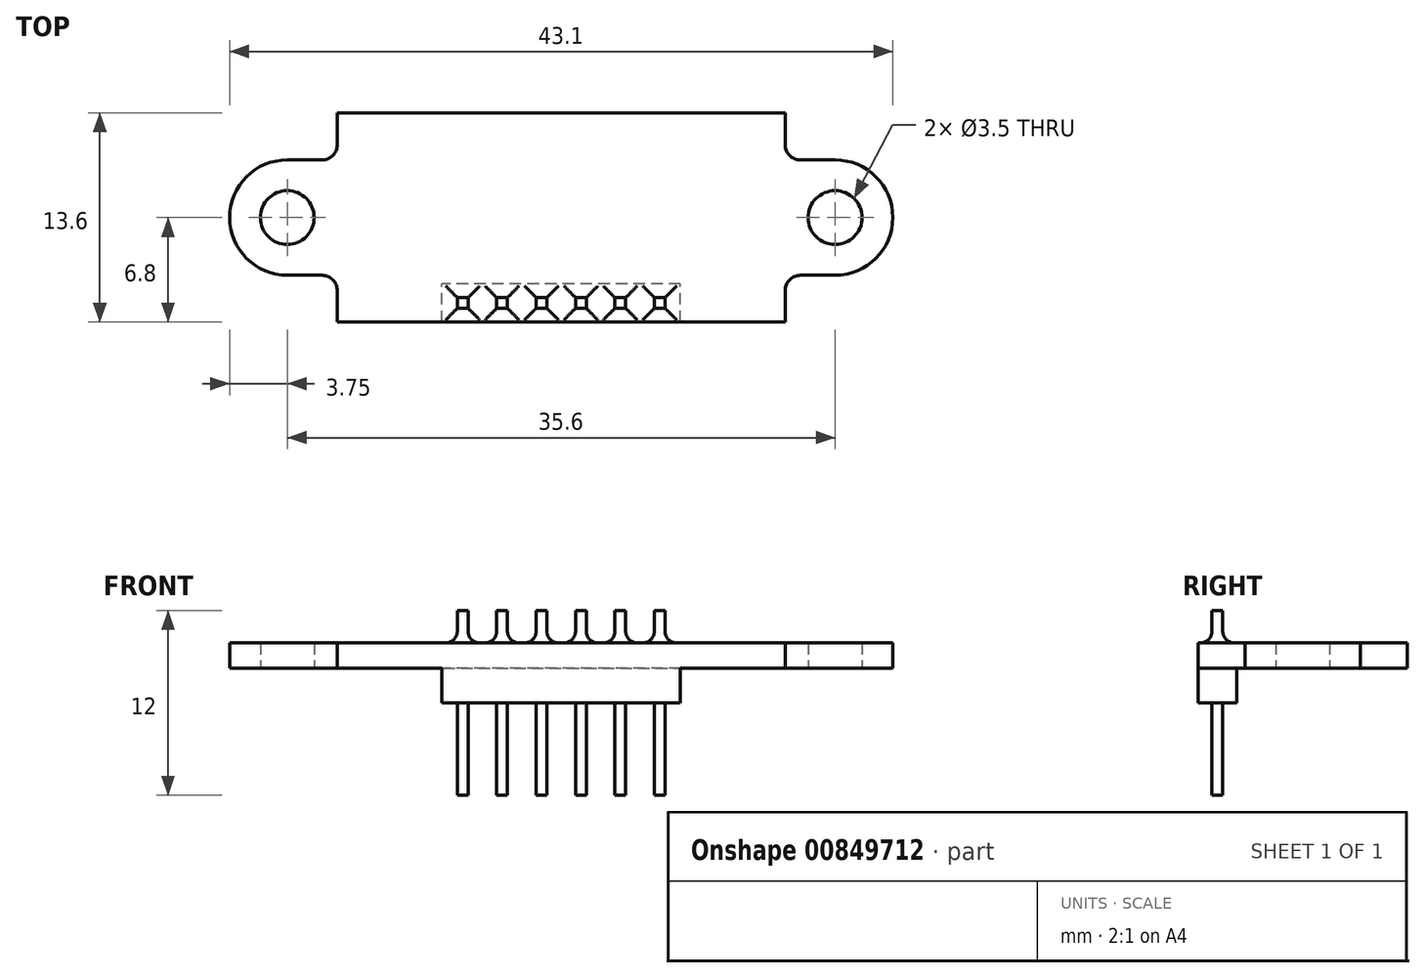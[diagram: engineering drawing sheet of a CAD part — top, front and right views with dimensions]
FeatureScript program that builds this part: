
annotation { "Feature Type Name" : "Feature", "Feature Type Description" : "" }
export const myFeature = defineFeature(function(context is Context, id is Id, definition is map)
    precondition{}
    {
        {
            var Q0;
            Q0=qCreatedBy(makeId("Top.planeOp"),FACE);
            var sketch = newSketch(context, id + "F0", { "sketchPlane" : qUnion([Q0])});
            skLineSegment(sketch, "E0.bottom", {"start": v(-14.55, 6.8) * mm, "end": v(14.55, 6.8) * mm});
            skLineSegment(sketch, "E0.top", {"start": v(-14.55, -6.8) * mm, "end": v(14.55, -6.8) * mm});
            skLineSegment(sketch, "E0.left", {"start": v(-14.55, 6.8) * mm, "end": v(-14.55, -6.8) * mm});
            skLineSegment(sketch, "E0.right", {"start": v(14.55, 6.8) * mm, "end": v(14.55, -6.8) * mm});
            skPoint(sketch, "E0.middle", {"position": v(0, 0) * mm});
            skCircle(sketch, "E1", {"center": v(17.8, 0) * mm, "radius": 1.75 * mm});
            skCircle(sketch, "E2", {"center": v(17.8, 0) * mm, "radius": 3.75 * mm});
            skLineSegment(sketch, "E3", {"start": v(17.8, 0) * mm, "end": v(0, 0) * mm, "construction": true});
            skLineSegment(sketch, "E4", {"start": v(14.55, 0) * mm, "end": v(21.55, 0) * mm, "construction": true});
            skLineSegment(sketch, "E5", {"start": v(17.8, 0) * mm, "end": v(17.8, 3.75) * mm, "construction": true});
            skLineSegment(sketch, "E6", {"start": v(17.8, 3.75) * mm, "end": v(14.55, 3.75) * mm});
            skLineSegment(sketch, "E7", {"start": v(14.55, 3.75) * mm, "end": v(14.6, 4.04) * mm, "construction": true});
            skLineSegment(sketch, "E8.MirrorCS", {"start": v(17.8, -3.75) * mm, "end": v(14.55, -3.75) * mm});
            skLineSegment(sketch, "E9", {"start": v(0, 6.8) * mm, "end": v(0, -6.8) * mm, "construction": true});
            skLineSegment(sketch, "E10.MirrorCS", {"start": v(-17.8, 3.75) * mm, "end": v(-14.55, 3.75) * mm});
            skCircle(sketch, "E11.MirrorC", {"center": v(-17.8, 0) * mm, "radius": 3.75 * mm});
            skCircle(sketch, "E12.MirrorC", {"center": v(-17.8, 0) * mm, "radius": 1.75 * mm});
            skLineSegment(sketch, "E13.MirrorCS", {"start": v(-17.8, -3.75) * mm, "end": v(-14.55, -3.75) * mm});
            skSolve(sketch);
        }
        {
            var Q0;
            Q0 = qSketchRegion(id + "F0", true);
            var Q1;
            {var subQ0=sQuery(id+"F0.wireOp",EDGE,"E11.MirrorC");var subQ1=sQuery(id+"F0.wireOp",EDGE,"E0.left");var subQ2=makeQuery(id+"F0.imprint","INTERSECT",VERTEX,{"disambiguationData":[OD(0.0)],"derivedFrom":[subQ1,subQ0]});Q1=makeQuery(id+"F0.imprint","IMPRINT",FACE,{"disambiguationData":[TD([[makeQuery(id+"F0.imprint","IMPRINT",EDGE,{"disambiguationData":[TD([[subQ2,-1.0]])],"derivedFrom":subQ1}),1.0]])]});}
            var Q2;
            {var subQ0=sQuery(id+"F0.wireOp",EDGE,"E2");var subQ1=sQuery(id+"F0.wireOp",EDGE,"E0.right");var subQ2=makeQuery(id+"F0.imprint","INTERSECT",VERTEX,{"disambiguationData":[OD(0.0)],"derivedFrom":[subQ1,subQ0]});Q2=makeQuery(id+"F0.imprint","IMPRINT",FACE,{"disambiguationData":[TD([[makeQuery(id+"F0.imprint","IMPRINT",EDGE,{"disambiguationData":[TD([[subQ2,-1.0]])],"derivedFrom":subQ1}),-1.0]])]});}
            extrude(context, id + "F1", {"entities" : qUnion([Q0, Q1, Q2]), "depth" : 1.65 * mm, "offsetDistance" : 25 * mm});
        }
        {
            var Q0;
            Q0=makeQuery(id+"F1.opExtrude","SWEPT_EDGE",EDGE,{"disambiguationData":[OSD([sQuery(id+"F0.wireOp",EDGE,"E0.right"),sQuery(id+"F0.wireOp",EDGE,"E6")])]});
            var Q1;
            Q1=makeQuery(id+"F1.opExtrude","SWEPT_EDGE",EDGE,{"disambiguationData":[OSD([sQuery(id+"F0.wireOp",EDGE,"E0.right"),sQuery(id+"F0.wireOp",EDGE,"E8.MirrorCS")])]});
            var Q2;
            Q2=makeQuery(id+"F1.opExtrude","SWEPT_EDGE",EDGE,{"disambiguationData":[OSD([sQuery(id+"F0.wireOp",EDGE,"E0.left"),sQuery(id+"F0.wireOp",EDGE,"E13.MirrorCS")])]});
            var Q3;
            Q3=makeQuery(id+"F1.opExtrude","SWEPT_EDGE",EDGE,{"disambiguationData":[OSD([sQuery(id+"F0.wireOp",EDGE,"E0.left"),sQuery(id+"F0.wireOp",EDGE,"E10.MirrorCS")])]});
            fillet(context, id + "F2", {"entities" : qUnion([Q0, Q1, Q2, Q3]), "radius" : 1 * mm, "tangentPropagation" : true, "allowEdgeOverflow" : false});
        }
        {
            var Q0;
            Q0=makeQuery(id+"F1.opExtrude","CAP_FACE",FACE,{"disambiguationData":[OSD([sQuery(id+"F0.wireOp",EDGE,"E0.bottom"),sQuery(id+"F0.wireOp",EDGE,"E0.top"),sQuery(id+"F0.wireOp",EDGE,"E0.left"),sQuery(id+"F0.wireOp",EDGE,"E0.right"),sQuery(id+"F0.wireOp",EDGE,"E1"),sQuery(id+"F0.wireOp",EDGE,"E2"),sQuery(id+"F0.wireOp",EDGE,"E6"),sQuery(id+"F0.wireOp",EDGE,"E8.MirrorCS"),sQuery(id+"F0.wireOp",EDGE,"E10.MirrorCS"),sQuery(id+"F0.wireOp",EDGE,"E11.MirrorC"),sQuery(id+"F0.wireOp",EDGE,"E12.MirrorC"),sQuery(id+"F0.wireOp",EDGE,"E13.MirrorCS")])],"isStart":true});
            var sketch = newSketch(context, id + "F3", { "sketchPlane" : qUnion([Q0])});
            skLineSegment(sketch, "E14", {"start": v(14.55, 6.8) * mm, "end": v(7.75, 6.8) * mm});
            skLineSegment(sketch, "E15.bottom", {"start": v(7.75, 6.8) * mm, "end": v(-7.75, 6.8) * mm});
            skLineSegment(sketch, "E15.top", {"start": v(7.75, 4.3) * mm, "end": v(-7.75, 4.3) * mm});
            skLineSegment(sketch, "E15.left", {"start": v(7.75, 6.8) * mm, "end": v(7.75, 4.3) * mm});
            skLineSegment(sketch, "E15.right", {"start": v(-7.75, 6.8) * mm, "end": v(-7.75, 4.3) * mm});
            skLineSegment(sketch, "E16", {"start": v(-14.55, 6.8) * mm, "end": v(-7.75, 6.8) * mm});
            skSolve(sketch);
        }
        {
            var Q0;
            Q0 = qSketchRegion(id + "F3", true);
            extrude(context, id + "F4", {"entities" : qUnion([Q0]), "operationType" : NewBodyOperationType.ADD, "depth" : 2.25 * mm, "offsetDistance" : 25 * mm});
        }
        {
            var Q0;
            Q0=makeQuery(id+"F4.opExtrude","CAP_FACE",FACE,{"disambiguationData":[OSD([sQuery(id+"F3.wireOp",EDGE,"E15.bottom"),sQuery(id+"F3.wireOp",EDGE,"E15.top"),sQuery(id+"F3.wireOp",EDGE,"E15.left"),sQuery(id+"F3.wireOp",EDGE,"E15.right")])],"isStart":false});
            var sketch = newSketch(context, id + "F5", { "sketchPlane" : qUnion([Q0])});
            skLineSegment(sketch, "E17.bottom", {"start": v(-6.05, 5.9) * mm, "end": v(-6.75, 5.9) * mm});
            skLineSegment(sketch, "E17.top", {"start": v(-6.05, 5.2) * mm, "end": v(-6.75, 5.2) * mm});
            skLineSegment(sketch, "E17.left", {"start": v(-6.05, 5.9) * mm, "end": v(-6.05, 5.2) * mm});
            skLineSegment(sketch, "E17.right", {"start": v(-6.75, 5.9) * mm, "end": v(-6.75, 5.2) * mm});
            skPoint(sketch, "E17.middle", {"position": v(-6.4, 5.55) * mm});
            skLineSegment(sketch, "E18.1.0.0", {"start": v(6.75, 5.9) * mm, "end": v(6.05, 5.9) * mm});
            skLineSegment(sketch, "E18.1.0.1", {"start": v(6.75, 5.9) * mm, "end": v(6.75, 5.2) * mm});
            skLineSegment(sketch, "E18.1.0.2", {"start": v(6.75, 5.2) * mm, "end": v(6.05, 5.2) * mm});
            skLineSegment(sketch, "E18.1.0.3", {"start": v(6.05, 5.9) * mm, "end": v(6.05, 5.2) * mm});
            skLineSegment(sketch, "E19", {"start": v(6.75, 5.55) * mm, "end": v(7.75, 5.55) * mm, "construction": true});
            skLineSegment(sketch, "E20", {"start": v(-6.75, 5.55) * mm, "end": v(-7.75, 5.55) * mm, "construction": true});
            skLineSegment(sketch, "E21.1.0.0", {"start": v(-3.49, 5.9) * mm, "end": v(-4.19, 5.9) * mm});
            skLineSegment(sketch, "E21.1.0.1", {"start": v(-4.19, 5.9) * mm, "end": v(-4.19, 5.2) * mm});
            skLineSegment(sketch, "E21.1.0.2", {"start": v(-3.49, 5.2) * mm, "end": v(-4.19, 5.2) * mm});
            skLineSegment(sketch, "E21.1.0.3", {"start": v(-3.49, 5.9) * mm, "end": v(-3.49, 5.2) * mm});
            skLineSegment(sketch, "E21.2.0.0", {"start": v(-0.93, 5.9) * mm, "end": v(-1.63, 5.9) * mm});
            skLineSegment(sketch, "E21.2.0.1", {"start": v(-1.63, 5.9) * mm, "end": v(-1.63, 5.2) * mm});
            skLineSegment(sketch, "E21.2.0.2", {"start": v(-0.93, 5.2) * mm, "end": v(-1.63, 5.2) * mm});
            skLineSegment(sketch, "E21.2.0.3", {"start": v(-0.93, 5.9) * mm, "end": v(-0.93, 5.2) * mm});
            skLineSegment(sketch, "E21.3.0.0", {"start": v(1.63, 5.9) * mm, "end": v(0.93, 5.9) * mm});
            skLineSegment(sketch, "E21.3.0.1", {"start": v(0.93, 5.9) * mm, "end": v(0.93, 5.2) * mm});
            skLineSegment(sketch, "E21.3.0.2", {"start": v(1.63, 5.2) * mm, "end": v(0.93, 5.2) * mm});
            skLineSegment(sketch, "E21.3.0.3", {"start": v(1.63, 5.9) * mm, "end": v(1.63, 5.2) * mm});
            skLineSegment(sketch, "E21.4.0.0", {"start": v(4.2, 5.9) * mm, "end": v(3.5, 5.9) * mm});
            skLineSegment(sketch, "E21.4.0.1", {"start": v(3.5, 5.9) * mm, "end": v(3.5, 5.2) * mm});
            skLineSegment(sketch, "E21.4.0.2", {"start": v(4.2, 5.2) * mm, "end": v(3.5, 5.2) * mm});
            skLineSegment(sketch, "E21.4.0.3", {"start": v(4.2, 5.9) * mm, "end": v(4.2, 5.2) * mm});
            skLineSegment(sketch, "E22", {"start": v(-3.49, 5.9) * mm, "end": v(-1.63, 5.9) * mm, "construction": true});
            skLineSegment(sketch, "E23", {"start": v(1.63, 5.9) * mm, "end": v(3.5, 5.9) * mm, "construction": true});
            skLineSegment(sketch, "E24", {"start": v(6.05, 5.9) * mm, "end": v(4.2, 5.9) * mm, "construction": true});
            skLineSegment(sketch, "E25", {"start": v(-0.93, 5.9) * mm, "end": v(0.93, 5.9) * mm, "construction": true});
            skLineSegment(sketch, "E26", {"start": v(-6.05, 5.9) * mm, "end": v(-4.19, 5.9) * mm, "construction": true});
            skSolve(sketch);
        }
        {
            var Q0;
            Q0 = qSketchRegion(id + "F5", true);
            extrude(context, id + "F6", {"entities" : qUnion([Q0]), "operationType" : NewBodyOperationType.ADD, "depth" : 6 * mm, "offsetDistance" : 25 * mm, "hasSecondDirection" : true, "secondDirectionOppositeDirection" : true, "secondDirectionDepth" : 6 * mm});
        }
        {
            var Q0;
            Q0=makeQuery(id+"F6.boolean.opBoolean","INTERSECT",EDGE,{"derivedFrom":[makeQuery(id+"F1.opExtrude","CAP_FACE",FACE,{"disambiguationData":[OSD([sQuery(id+"F0.wireOp",EDGE,"E0.bottom"),sQuery(id+"F0.wireOp",EDGE,"E0.top"),sQuery(id+"F0.wireOp",EDGE,"E0.left"),sQuery(id+"F0.wireOp",EDGE,"E0.right"),sQuery(id+"F0.wireOp",EDGE,"E1"),sQuery(id+"F0.wireOp",EDGE,"E2"),sQuery(id+"F0.wireOp",EDGE,"E6"),sQuery(id+"F0.wireOp",EDGE,"E8.MirrorCS"),sQuery(id+"F0.wireOp",EDGE,"E10.MirrorCS"),sQuery(id+"F0.wireOp",EDGE,"E11.MirrorC"),sQuery(id+"F0.wireOp",EDGE,"E12.MirrorC"),sQuery(id+"F0.wireOp",EDGE,"E13.MirrorCS")])],"isStart":false}),makeQuery(id+"F6.opExtrude","SWEPT_FACE",FACE,{"disambiguationData":[OSD([sQuery(id+"F5.wireOp",EDGE,"E18.1.0.2")])]})]});
            var Q1;
            Q1=makeQuery(id+"F6.boolean.opBoolean","INTERSECT",EDGE,{"derivedFrom":[makeQuery(id+"F1.opExtrude","CAP_FACE",FACE,{"disambiguationData":[OSD([sQuery(id+"F0.wireOp",EDGE,"E0.bottom"),sQuery(id+"F0.wireOp",EDGE,"E0.top"),sQuery(id+"F0.wireOp",EDGE,"E0.left"),sQuery(id+"F0.wireOp",EDGE,"E0.right"),sQuery(id+"F0.wireOp",EDGE,"E1"),sQuery(id+"F0.wireOp",EDGE,"E2"),sQuery(id+"F0.wireOp",EDGE,"E6"),sQuery(id+"F0.wireOp",EDGE,"E8.MirrorCS"),sQuery(id+"F0.wireOp",EDGE,"E10.MirrorCS"),sQuery(id+"F0.wireOp",EDGE,"E11.MirrorC"),sQuery(id+"F0.wireOp",EDGE,"E12.MirrorC"),sQuery(id+"F0.wireOp",EDGE,"E13.MirrorCS")])],"isStart":false}),makeQuery(id+"F6.opExtrude","SWEPT_FACE",FACE,{"disambiguationData":[OSD([sQuery(id+"F5.wireOp",EDGE,"E18.1.0.1")])]})]});
            var Q2;
            Q2=makeQuery(id+"F6.boolean.opBoolean","INTERSECT",EDGE,{"derivedFrom":[makeQuery(id+"F1.opExtrude","CAP_FACE",FACE,{"disambiguationData":[OSD([sQuery(id+"F0.wireOp",EDGE,"E0.bottom"),sQuery(id+"F0.wireOp",EDGE,"E0.top"),sQuery(id+"F0.wireOp",EDGE,"E0.left"),sQuery(id+"F0.wireOp",EDGE,"E0.right"),sQuery(id+"F0.wireOp",EDGE,"E1"),sQuery(id+"F0.wireOp",EDGE,"E2"),sQuery(id+"F0.wireOp",EDGE,"E6"),sQuery(id+"F0.wireOp",EDGE,"E8.MirrorCS"),sQuery(id+"F0.wireOp",EDGE,"E10.MirrorCS"),sQuery(id+"F0.wireOp",EDGE,"E11.MirrorC"),sQuery(id+"F0.wireOp",EDGE,"E12.MirrorC"),sQuery(id+"F0.wireOp",EDGE,"E13.MirrorCS")])],"isStart":false}),makeQuery(id+"F6.opExtrude","SWEPT_FACE",FACE,{"disambiguationData":[OSD([sQuery(id+"F5.wireOp",EDGE,"E18.1.0.0")])]})]});
            var Q3;
            Q3=makeQuery(id+"F6.boolean.opBoolean","INTERSECT",EDGE,{"derivedFrom":[makeQuery(id+"F1.opExtrude","CAP_FACE",FACE,{"disambiguationData":[OSD([sQuery(id+"F0.wireOp",EDGE,"E0.bottom"),sQuery(id+"F0.wireOp",EDGE,"E0.top"),sQuery(id+"F0.wireOp",EDGE,"E0.left"),sQuery(id+"F0.wireOp",EDGE,"E0.right"),sQuery(id+"F0.wireOp",EDGE,"E1"),sQuery(id+"F0.wireOp",EDGE,"E2"),sQuery(id+"F0.wireOp",EDGE,"E6"),sQuery(id+"F0.wireOp",EDGE,"E8.MirrorCS"),sQuery(id+"F0.wireOp",EDGE,"E10.MirrorCS"),sQuery(id+"F0.wireOp",EDGE,"E11.MirrorC"),sQuery(id+"F0.wireOp",EDGE,"E12.MirrorC"),sQuery(id+"F0.wireOp",EDGE,"E13.MirrorCS")])],"isStart":false}),makeQuery(id+"F6.opExtrude","SWEPT_FACE",FACE,{"disambiguationData":[OSD([sQuery(id+"F5.wireOp",EDGE,"E18.1.0.3")])]})]});
            var Q4;
            Q4=makeQuery(id+"F6.boolean.opBoolean","INTERSECT",EDGE,{"derivedFrom":[makeQuery(id+"F1.opExtrude","CAP_FACE",FACE,{"disambiguationData":[OSD([sQuery(id+"F0.wireOp",EDGE,"E0.bottom"),sQuery(id+"F0.wireOp",EDGE,"E0.top"),sQuery(id+"F0.wireOp",EDGE,"E0.left"),sQuery(id+"F0.wireOp",EDGE,"E0.right"),sQuery(id+"F0.wireOp",EDGE,"E1"),sQuery(id+"F0.wireOp",EDGE,"E2"),sQuery(id+"F0.wireOp",EDGE,"E6"),sQuery(id+"F0.wireOp",EDGE,"E8.MirrorCS"),sQuery(id+"F0.wireOp",EDGE,"E10.MirrorCS"),sQuery(id+"F0.wireOp",EDGE,"E11.MirrorC"),sQuery(id+"F0.wireOp",EDGE,"E12.MirrorC"),sQuery(id+"F0.wireOp",EDGE,"E13.MirrorCS")])],"isStart":false}),makeQuery(id+"F6.opExtrude","SWEPT_FACE",FACE,{"disambiguationData":[OSD([sQuery(id+"F5.wireOp",EDGE,"E21.4.0.3")])]})]});
            var Q5;
            Q5=makeQuery(id+"F6.boolean.opBoolean","INTERSECT",EDGE,{"derivedFrom":[makeQuery(id+"F1.opExtrude","CAP_FACE",FACE,{"disambiguationData":[OSD([sQuery(id+"F0.wireOp",EDGE,"E0.bottom"),sQuery(id+"F0.wireOp",EDGE,"E0.top"),sQuery(id+"F0.wireOp",EDGE,"E0.left"),sQuery(id+"F0.wireOp",EDGE,"E0.right"),sQuery(id+"F0.wireOp",EDGE,"E1"),sQuery(id+"F0.wireOp",EDGE,"E2"),sQuery(id+"F0.wireOp",EDGE,"E6"),sQuery(id+"F0.wireOp",EDGE,"E8.MirrorCS"),sQuery(id+"F0.wireOp",EDGE,"E10.MirrorCS"),sQuery(id+"F0.wireOp",EDGE,"E11.MirrorC"),sQuery(id+"F0.wireOp",EDGE,"E12.MirrorC"),sQuery(id+"F0.wireOp",EDGE,"E13.MirrorCS")])],"isStart":false}),makeQuery(id+"F6.opExtrude","SWEPT_FACE",FACE,{"disambiguationData":[OSD([sQuery(id+"F5.wireOp",EDGE,"E21.4.0.0")])]})]});
            var Q6;
            Q6=makeQuery(id+"F6.boolean.opBoolean","INTERSECT",EDGE,{"derivedFrom":[makeQuery(id+"F1.opExtrude","CAP_FACE",FACE,{"disambiguationData":[OSD([sQuery(id+"F0.wireOp",EDGE,"E0.bottom"),sQuery(id+"F0.wireOp",EDGE,"E0.top"),sQuery(id+"F0.wireOp",EDGE,"E0.left"),sQuery(id+"F0.wireOp",EDGE,"E0.right"),sQuery(id+"F0.wireOp",EDGE,"E1"),sQuery(id+"F0.wireOp",EDGE,"E2"),sQuery(id+"F0.wireOp",EDGE,"E6"),sQuery(id+"F0.wireOp",EDGE,"E8.MirrorCS"),sQuery(id+"F0.wireOp",EDGE,"E10.MirrorCS"),sQuery(id+"F0.wireOp",EDGE,"E11.MirrorC"),sQuery(id+"F0.wireOp",EDGE,"E12.MirrorC"),sQuery(id+"F0.wireOp",EDGE,"E13.MirrorCS")])],"isStart":false}),makeQuery(id+"F6.opExtrude","SWEPT_FACE",FACE,{"disambiguationData":[OSD([sQuery(id+"F5.wireOp",EDGE,"E21.4.0.1")])]})]});
            var Q7;
            Q7=makeQuery(id+"F6.boolean.opBoolean","INTERSECT",EDGE,{"derivedFrom":[makeQuery(id+"F1.opExtrude","CAP_FACE",FACE,{"disambiguationData":[OSD([sQuery(id+"F0.wireOp",EDGE,"E0.bottom"),sQuery(id+"F0.wireOp",EDGE,"E0.top"),sQuery(id+"F0.wireOp",EDGE,"E0.left"),sQuery(id+"F0.wireOp",EDGE,"E0.right"),sQuery(id+"F0.wireOp",EDGE,"E1"),sQuery(id+"F0.wireOp",EDGE,"E2"),sQuery(id+"F0.wireOp",EDGE,"E6"),sQuery(id+"F0.wireOp",EDGE,"E8.MirrorCS"),sQuery(id+"F0.wireOp",EDGE,"E10.MirrorCS"),sQuery(id+"F0.wireOp",EDGE,"E11.MirrorC"),sQuery(id+"F0.wireOp",EDGE,"E12.MirrorC"),sQuery(id+"F0.wireOp",EDGE,"E13.MirrorCS")])],"isStart":false}),makeQuery(id+"F6.opExtrude","SWEPT_FACE",FACE,{"disambiguationData":[OSD([sQuery(id+"F5.wireOp",EDGE,"E21.4.0.2")])]})]});
            var Q8;
            Q8=makeQuery(id+"F6.boolean.opBoolean","INTERSECT",EDGE,{"derivedFrom":[makeQuery(id+"F1.opExtrude","CAP_FACE",FACE,{"disambiguationData":[OSD([sQuery(id+"F0.wireOp",EDGE,"E0.bottom"),sQuery(id+"F0.wireOp",EDGE,"E0.top"),sQuery(id+"F0.wireOp",EDGE,"E0.left"),sQuery(id+"F0.wireOp",EDGE,"E0.right"),sQuery(id+"F0.wireOp",EDGE,"E1"),sQuery(id+"F0.wireOp",EDGE,"E2"),sQuery(id+"F0.wireOp",EDGE,"E6"),sQuery(id+"F0.wireOp",EDGE,"E8.MirrorCS"),sQuery(id+"F0.wireOp",EDGE,"E10.MirrorCS"),sQuery(id+"F0.wireOp",EDGE,"E11.MirrorC"),sQuery(id+"F0.wireOp",EDGE,"E12.MirrorC"),sQuery(id+"F0.wireOp",EDGE,"E13.MirrorCS")])],"isStart":false}),makeQuery(id+"F6.opExtrude","SWEPT_FACE",FACE,{"disambiguationData":[OSD([sQuery(id+"F5.wireOp",EDGE,"E21.3.0.2")])]})]});
            var Q9;
            Q9=makeQuery(id+"F6.boolean.opBoolean","INTERSECT",EDGE,{"derivedFrom":[makeQuery(id+"F1.opExtrude","CAP_FACE",FACE,{"disambiguationData":[OSD([sQuery(id+"F0.wireOp",EDGE,"E0.bottom"),sQuery(id+"F0.wireOp",EDGE,"E0.top"),sQuery(id+"F0.wireOp",EDGE,"E0.left"),sQuery(id+"F0.wireOp",EDGE,"E0.right"),sQuery(id+"F0.wireOp",EDGE,"E1"),sQuery(id+"F0.wireOp",EDGE,"E2"),sQuery(id+"F0.wireOp",EDGE,"E6"),sQuery(id+"F0.wireOp",EDGE,"E8.MirrorCS"),sQuery(id+"F0.wireOp",EDGE,"E10.MirrorCS"),sQuery(id+"F0.wireOp",EDGE,"E11.MirrorC"),sQuery(id+"F0.wireOp",EDGE,"E12.MirrorC"),sQuery(id+"F0.wireOp",EDGE,"E13.MirrorCS")])],"isStart":false}),makeQuery(id+"F6.opExtrude","SWEPT_FACE",FACE,{"disambiguationData":[OSD([sQuery(id+"F5.wireOp",EDGE,"E21.3.0.1")])]})]});
            var Q10;
            Q10=makeQuery(id+"F6.boolean.opBoolean","INTERSECT",EDGE,{"derivedFrom":[makeQuery(id+"F1.opExtrude","CAP_FACE",FACE,{"disambiguationData":[OSD([sQuery(id+"F0.wireOp",EDGE,"E0.bottom"),sQuery(id+"F0.wireOp",EDGE,"E0.top"),sQuery(id+"F0.wireOp",EDGE,"E0.left"),sQuery(id+"F0.wireOp",EDGE,"E0.right"),sQuery(id+"F0.wireOp",EDGE,"E1"),sQuery(id+"F0.wireOp",EDGE,"E2"),sQuery(id+"F0.wireOp",EDGE,"E6"),sQuery(id+"F0.wireOp",EDGE,"E8.MirrorCS"),sQuery(id+"F0.wireOp",EDGE,"E10.MirrorCS"),sQuery(id+"F0.wireOp",EDGE,"E11.MirrorC"),sQuery(id+"F0.wireOp",EDGE,"E12.MirrorC"),sQuery(id+"F0.wireOp",EDGE,"E13.MirrorCS")])],"isStart":false}),makeQuery(id+"F6.opExtrude","SWEPT_FACE",FACE,{"disambiguationData":[OSD([sQuery(id+"F5.wireOp",EDGE,"E21.3.0.0")])]})]});
            var Q11;
            Q11=makeQuery(id+"F6.boolean.opBoolean","INTERSECT",EDGE,{"derivedFrom":[makeQuery(id+"F1.opExtrude","CAP_FACE",FACE,{"disambiguationData":[OSD([sQuery(id+"F0.wireOp",EDGE,"E0.bottom"),sQuery(id+"F0.wireOp",EDGE,"E0.top"),sQuery(id+"F0.wireOp",EDGE,"E0.left"),sQuery(id+"F0.wireOp",EDGE,"E0.right"),sQuery(id+"F0.wireOp",EDGE,"E1"),sQuery(id+"F0.wireOp",EDGE,"E2"),sQuery(id+"F0.wireOp",EDGE,"E6"),sQuery(id+"F0.wireOp",EDGE,"E8.MirrorCS"),sQuery(id+"F0.wireOp",EDGE,"E10.MirrorCS"),sQuery(id+"F0.wireOp",EDGE,"E11.MirrorC"),sQuery(id+"F0.wireOp",EDGE,"E12.MirrorC"),sQuery(id+"F0.wireOp",EDGE,"E13.MirrorCS")])],"isStart":false}),makeQuery(id+"F6.opExtrude","SWEPT_FACE",FACE,{"disambiguationData":[OSD([sQuery(id+"F5.wireOp",EDGE,"E21.3.0.3")])]})]});
            var Q12;
            Q12=makeQuery(id+"F6.boolean.opBoolean","INTERSECT",EDGE,{"derivedFrom":[makeQuery(id+"F1.opExtrude","CAP_FACE",FACE,{"disambiguationData":[OSD([sQuery(id+"F0.wireOp",EDGE,"E0.bottom"),sQuery(id+"F0.wireOp",EDGE,"E0.top"),sQuery(id+"F0.wireOp",EDGE,"E0.left"),sQuery(id+"F0.wireOp",EDGE,"E0.right"),sQuery(id+"F0.wireOp",EDGE,"E1"),sQuery(id+"F0.wireOp",EDGE,"E2"),sQuery(id+"F0.wireOp",EDGE,"E6"),sQuery(id+"F0.wireOp",EDGE,"E8.MirrorCS"),sQuery(id+"F0.wireOp",EDGE,"E10.MirrorCS"),sQuery(id+"F0.wireOp",EDGE,"E11.MirrorC"),sQuery(id+"F0.wireOp",EDGE,"E12.MirrorC"),sQuery(id+"F0.wireOp",EDGE,"E13.MirrorCS")])],"isStart":false}),makeQuery(id+"F6.opExtrude","SWEPT_FACE",FACE,{"disambiguationData":[OSD([sQuery(id+"F5.wireOp",EDGE,"E21.2.0.0")])]})]});
            var Q13;
            Q13=makeQuery(id+"F6.boolean.opBoolean","INTERSECT",EDGE,{"derivedFrom":[makeQuery(id+"F1.opExtrude","CAP_FACE",FACE,{"disambiguationData":[OSD([sQuery(id+"F0.wireOp",EDGE,"E0.bottom"),sQuery(id+"F0.wireOp",EDGE,"E0.top"),sQuery(id+"F0.wireOp",EDGE,"E0.left"),sQuery(id+"F0.wireOp",EDGE,"E0.right"),sQuery(id+"F0.wireOp",EDGE,"E1"),sQuery(id+"F0.wireOp",EDGE,"E2"),sQuery(id+"F0.wireOp",EDGE,"E6"),sQuery(id+"F0.wireOp",EDGE,"E8.MirrorCS"),sQuery(id+"F0.wireOp",EDGE,"E10.MirrorCS"),sQuery(id+"F0.wireOp",EDGE,"E11.MirrorC"),sQuery(id+"F0.wireOp",EDGE,"E12.MirrorC"),sQuery(id+"F0.wireOp",EDGE,"E13.MirrorCS")])],"isStart":false}),makeQuery(id+"F6.opExtrude","SWEPT_FACE",FACE,{"disambiguationData":[OSD([sQuery(id+"F5.wireOp",EDGE,"E21.2.0.1")])]})]});
            var Q14;
            Q14=makeQuery(id+"F6.boolean.opBoolean","INTERSECT",EDGE,{"derivedFrom":[makeQuery(id+"F1.opExtrude","CAP_FACE",FACE,{"disambiguationData":[OSD([sQuery(id+"F0.wireOp",EDGE,"E0.bottom"),sQuery(id+"F0.wireOp",EDGE,"E0.top"),sQuery(id+"F0.wireOp",EDGE,"E0.left"),sQuery(id+"F0.wireOp",EDGE,"E0.right"),sQuery(id+"F0.wireOp",EDGE,"E1"),sQuery(id+"F0.wireOp",EDGE,"E2"),sQuery(id+"F0.wireOp",EDGE,"E6"),sQuery(id+"F0.wireOp",EDGE,"E8.MirrorCS"),sQuery(id+"F0.wireOp",EDGE,"E10.MirrorCS"),sQuery(id+"F0.wireOp",EDGE,"E11.MirrorC"),sQuery(id+"F0.wireOp",EDGE,"E12.MirrorC"),sQuery(id+"F0.wireOp",EDGE,"E13.MirrorCS")])],"isStart":false}),makeQuery(id+"F6.opExtrude","SWEPT_FACE",FACE,{"disambiguationData":[OSD([sQuery(id+"F5.wireOp",EDGE,"E21.2.0.3")])]})]});
            var Q15;
            Q15=makeQuery(id+"F6.boolean.opBoolean","INTERSECT",EDGE,{"derivedFrom":[makeQuery(id+"F1.opExtrude","CAP_FACE",FACE,{"disambiguationData":[OSD([sQuery(id+"F0.wireOp",EDGE,"E0.bottom"),sQuery(id+"F0.wireOp",EDGE,"E0.top"),sQuery(id+"F0.wireOp",EDGE,"E0.left"),sQuery(id+"F0.wireOp",EDGE,"E0.right"),sQuery(id+"F0.wireOp",EDGE,"E1"),sQuery(id+"F0.wireOp",EDGE,"E2"),sQuery(id+"F0.wireOp",EDGE,"E6"),sQuery(id+"F0.wireOp",EDGE,"E8.MirrorCS"),sQuery(id+"F0.wireOp",EDGE,"E10.MirrorCS"),sQuery(id+"F0.wireOp",EDGE,"E11.MirrorC"),sQuery(id+"F0.wireOp",EDGE,"E12.MirrorC"),sQuery(id+"F0.wireOp",EDGE,"E13.MirrorCS")])],"isStart":false}),makeQuery(id+"F6.opExtrude","SWEPT_FACE",FACE,{"disambiguationData":[OSD([sQuery(id+"F5.wireOp",EDGE,"E21.2.0.2")])]})]});
            var Q16;
            Q16=makeQuery(id+"F6.boolean.opBoolean","INTERSECT",EDGE,{"derivedFrom":[makeQuery(id+"F1.opExtrude","CAP_FACE",FACE,{"disambiguationData":[OSD([sQuery(id+"F0.wireOp",EDGE,"E0.bottom"),sQuery(id+"F0.wireOp",EDGE,"E0.top"),sQuery(id+"F0.wireOp",EDGE,"E0.left"),sQuery(id+"F0.wireOp",EDGE,"E0.right"),sQuery(id+"F0.wireOp",EDGE,"E1"),sQuery(id+"F0.wireOp",EDGE,"E2"),sQuery(id+"F0.wireOp",EDGE,"E6"),sQuery(id+"F0.wireOp",EDGE,"E8.MirrorCS"),sQuery(id+"F0.wireOp",EDGE,"E10.MirrorCS"),sQuery(id+"F0.wireOp",EDGE,"E11.MirrorC"),sQuery(id+"F0.wireOp",EDGE,"E12.MirrorC"),sQuery(id+"F0.wireOp",EDGE,"E13.MirrorCS")])],"isStart":false}),makeQuery(id+"F6.opExtrude","SWEPT_FACE",FACE,{"disambiguationData":[OSD([sQuery(id+"F5.wireOp",EDGE,"E21.1.0.0")])]})]});
            var Q17;
            Q17=makeQuery(id+"F6.boolean.opBoolean","INTERSECT",EDGE,{"derivedFrom":[makeQuery(id+"F1.opExtrude","CAP_FACE",FACE,{"disambiguationData":[OSD([sQuery(id+"F0.wireOp",EDGE,"E0.bottom"),sQuery(id+"F0.wireOp",EDGE,"E0.top"),sQuery(id+"F0.wireOp",EDGE,"E0.left"),sQuery(id+"F0.wireOp",EDGE,"E0.right"),sQuery(id+"F0.wireOp",EDGE,"E1"),sQuery(id+"F0.wireOp",EDGE,"E2"),sQuery(id+"F0.wireOp",EDGE,"E6"),sQuery(id+"F0.wireOp",EDGE,"E8.MirrorCS"),sQuery(id+"F0.wireOp",EDGE,"E10.MirrorCS"),sQuery(id+"F0.wireOp",EDGE,"E11.MirrorC"),sQuery(id+"F0.wireOp",EDGE,"E12.MirrorC"),sQuery(id+"F0.wireOp",EDGE,"E13.MirrorCS")])],"isStart":false}),makeQuery(id+"F6.opExtrude","SWEPT_FACE",FACE,{"disambiguationData":[OSD([sQuery(id+"F5.wireOp",EDGE,"E21.1.0.1")])]})]});
            var Q18;
            Q18=makeQuery(id+"F6.boolean.opBoolean","INTERSECT",EDGE,{"derivedFrom":[makeQuery(id+"F1.opExtrude","CAP_FACE",FACE,{"disambiguationData":[OSD([sQuery(id+"F0.wireOp",EDGE,"E0.bottom"),sQuery(id+"F0.wireOp",EDGE,"E0.top"),sQuery(id+"F0.wireOp",EDGE,"E0.left"),sQuery(id+"F0.wireOp",EDGE,"E0.right"),sQuery(id+"F0.wireOp",EDGE,"E1"),sQuery(id+"F0.wireOp",EDGE,"E2"),sQuery(id+"F0.wireOp",EDGE,"E6"),sQuery(id+"F0.wireOp",EDGE,"E8.MirrorCS"),sQuery(id+"F0.wireOp",EDGE,"E10.MirrorCS"),sQuery(id+"F0.wireOp",EDGE,"E11.MirrorC"),sQuery(id+"F0.wireOp",EDGE,"E12.MirrorC"),sQuery(id+"F0.wireOp",EDGE,"E13.MirrorCS")])],"isStart":false}),makeQuery(id+"F6.opExtrude","SWEPT_FACE",FACE,{"disambiguationData":[OSD([sQuery(id+"F5.wireOp",EDGE,"E21.1.0.3")])]})]});
            var Q19;
            Q19=makeQuery(id+"F6.boolean.opBoolean","INTERSECT",EDGE,{"derivedFrom":[makeQuery(id+"F1.opExtrude","CAP_FACE",FACE,{"disambiguationData":[OSD([sQuery(id+"F0.wireOp",EDGE,"E0.bottom"),sQuery(id+"F0.wireOp",EDGE,"E0.top"),sQuery(id+"F0.wireOp",EDGE,"E0.left"),sQuery(id+"F0.wireOp",EDGE,"E0.right"),sQuery(id+"F0.wireOp",EDGE,"E1"),sQuery(id+"F0.wireOp",EDGE,"E2"),sQuery(id+"F0.wireOp",EDGE,"E6"),sQuery(id+"F0.wireOp",EDGE,"E8.MirrorCS"),sQuery(id+"F0.wireOp",EDGE,"E10.MirrorCS"),sQuery(id+"F0.wireOp",EDGE,"E11.MirrorC"),sQuery(id+"F0.wireOp",EDGE,"E12.MirrorC"),sQuery(id+"F0.wireOp",EDGE,"E13.MirrorCS")])],"isStart":false}),makeQuery(id+"F6.opExtrude","SWEPT_FACE",FACE,{"disambiguationData":[OSD([sQuery(id+"F5.wireOp",EDGE,"E21.1.0.2")])]})]});
            var Q20;
            Q20=makeQuery(id+"F6.boolean.opBoolean","INTERSECT",EDGE,{"derivedFrom":[makeQuery(id+"F1.opExtrude","CAP_FACE",FACE,{"disambiguationData":[OSD([sQuery(id+"F0.wireOp",EDGE,"E0.bottom"),sQuery(id+"F0.wireOp",EDGE,"E0.top"),sQuery(id+"F0.wireOp",EDGE,"E0.left"),sQuery(id+"F0.wireOp",EDGE,"E0.right"),sQuery(id+"F0.wireOp",EDGE,"E1"),sQuery(id+"F0.wireOp",EDGE,"E2"),sQuery(id+"F0.wireOp",EDGE,"E6"),sQuery(id+"F0.wireOp",EDGE,"E8.MirrorCS"),sQuery(id+"F0.wireOp",EDGE,"E10.MirrorCS"),sQuery(id+"F0.wireOp",EDGE,"E11.MirrorC"),sQuery(id+"F0.wireOp",EDGE,"E12.MirrorC"),sQuery(id+"F0.wireOp",EDGE,"E13.MirrorCS")])],"isStart":false}),makeQuery(id+"F6.opExtrude","SWEPT_FACE",FACE,{"disambiguationData":[OSD([sQuery(id+"F5.wireOp",EDGE,"E17.top")])]})]});
            var Q21;
            Q21=makeQuery(id+"F6.boolean.opBoolean","INTERSECT",EDGE,{"derivedFrom":[makeQuery(id+"F1.opExtrude","CAP_FACE",FACE,{"disambiguationData":[OSD([sQuery(id+"F0.wireOp",EDGE,"E0.bottom"),sQuery(id+"F0.wireOp",EDGE,"E0.top"),sQuery(id+"F0.wireOp",EDGE,"E0.left"),sQuery(id+"F0.wireOp",EDGE,"E0.right"),sQuery(id+"F0.wireOp",EDGE,"E1"),sQuery(id+"F0.wireOp",EDGE,"E2"),sQuery(id+"F0.wireOp",EDGE,"E6"),sQuery(id+"F0.wireOp",EDGE,"E8.MirrorCS"),sQuery(id+"F0.wireOp",EDGE,"E10.MirrorCS"),sQuery(id+"F0.wireOp",EDGE,"E11.MirrorC"),sQuery(id+"F0.wireOp",EDGE,"E12.MirrorC"),sQuery(id+"F0.wireOp",EDGE,"E13.MirrorCS")])],"isStart":false}),makeQuery(id+"F6.opExtrude","SWEPT_FACE",FACE,{"disambiguationData":[OSD([sQuery(id+"F5.wireOp",EDGE,"E17.right")])]})]});
            var Q22;
            Q22=makeQuery(id+"F6.boolean.opBoolean","INTERSECT",EDGE,{"derivedFrom":[makeQuery(id+"F1.opExtrude","CAP_FACE",FACE,{"disambiguationData":[OSD([sQuery(id+"F0.wireOp",EDGE,"E0.bottom"),sQuery(id+"F0.wireOp",EDGE,"E0.top"),sQuery(id+"F0.wireOp",EDGE,"E0.left"),sQuery(id+"F0.wireOp",EDGE,"E0.right"),sQuery(id+"F0.wireOp",EDGE,"E1"),sQuery(id+"F0.wireOp",EDGE,"E2"),sQuery(id+"F0.wireOp",EDGE,"E6"),sQuery(id+"F0.wireOp",EDGE,"E8.MirrorCS"),sQuery(id+"F0.wireOp",EDGE,"E10.MirrorCS"),sQuery(id+"F0.wireOp",EDGE,"E11.MirrorC"),sQuery(id+"F0.wireOp",EDGE,"E12.MirrorC"),sQuery(id+"F0.wireOp",EDGE,"E13.MirrorCS")])],"isStart":false}),makeQuery(id+"F6.opExtrude","SWEPT_FACE",FACE,{"disambiguationData":[OSD([sQuery(id+"F5.wireOp",EDGE,"E17.bottom")])]})]});
            var Q23;
            Q23=makeQuery(id+"F6.boolean.opBoolean","INTERSECT",EDGE,{"derivedFrom":[makeQuery(id+"F1.opExtrude","CAP_FACE",FACE,{"disambiguationData":[OSD([sQuery(id+"F0.wireOp",EDGE,"E0.bottom"),sQuery(id+"F0.wireOp",EDGE,"E0.top"),sQuery(id+"F0.wireOp",EDGE,"E0.left"),sQuery(id+"F0.wireOp",EDGE,"E0.right"),sQuery(id+"F0.wireOp",EDGE,"E1"),sQuery(id+"F0.wireOp",EDGE,"E2"),sQuery(id+"F0.wireOp",EDGE,"E6"),sQuery(id+"F0.wireOp",EDGE,"E8.MirrorCS"),sQuery(id+"F0.wireOp",EDGE,"E10.MirrorCS"),sQuery(id+"F0.wireOp",EDGE,"E11.MirrorC"),sQuery(id+"F0.wireOp",EDGE,"E12.MirrorC"),sQuery(id+"F0.wireOp",EDGE,"E13.MirrorCS")])],"isStart":false}),makeQuery(id+"F6.opExtrude","SWEPT_FACE",FACE,{"disambiguationData":[OSD([sQuery(id+"F5.wireOp",EDGE,"E17.left")])]})]});
            fillet(context, id + "F7", {"entities" : qUnion([Q0, Q1, Q2, Q3, Q4, Q5, Q6, Q7, Q8, Q9, Q10, Q11, Q12, Q13, Q14, Q15, Q16, Q17, Q18, Q19, Q20, Q21, Q22, Q23]), "radius" : .75 * mm, "tangentPropagation" : true, "allowEdgeOverflow" : false});
        }
    });
